# Revit family: Холодильные столы низкотемпературные
name_source: partatom
category: Оборудование
units: mm (PartAtom-declared; Revit-internal decimal feet)

## family parameters
Всегда вертикально = Да
Классификация = Нет
На основе рабочей плоскости = Нет
Общий = Нет
При загрузке вырезать с полостями = Нет
Размер круглого соединителя = Использовать диаметр
Тип детали = Нормальный
Точка расчета площади = Нет

## types (12) — shared parameters
Высота = 850 мм
Диап. рабочих темп. = -18
Напряжение питания = 230.00 В
Степень защиты = IP24
Терморегулятор = эл. блок
Тип оттайки = авт. с системой исп. конденсата
Тип охлаждения = динамический
Хладаген = R404A
Холодильный стол = нержавеющая сталь
zero-valued in all types: Отметка по умолчанию

## per-type parameters (varying)
| type | Боковая панель упр. | Боковая панель упр. (3 решетки) | Вес нетто/брутто, кг | Габаритные размеры, мм | Глубина | Дверь G - 1 | Дверь G-2 | Дверь G-3 | Дверь G-4 | Дверь GC | Количество дверей | Нижнее распол Дверь -1 | Нижнее распол. Дверь -2 | Нижняя панель упр. | Объем, л | Размеры в упоковке, мм | Столешница закругл. | Столешница квадр. | Таблица поиска | Условия окр. среды (темп/влажн) | Цена, руб | Число дверей | Ширина |
| TB4GN-GC | Да | Нет | 165/200 | 2060х705х850/910 | 705 мм | Нет | Нет | Нет | Нет | Да | 4 | Нет | Нет | Нет | 600 | 2165х815х1045 | Нет | Да | ТB | до +43/до 80 | 96 366 | 4 | 2060 мм |
| TBi4-G | Нет | Нет | - | 1850х600х850/910 | 600 мм | Нет | Нет | Нет | Нет | Нет | 4 | Да | Да | Да | 306 | 2000х714х1040 | Да | Нет | ТB | до +32 | 90 200 | 2 | 1850 мм |
| TBi-2G | Нет | Нет | - | 900х600х850/910 | 600 мм | Нет | Нет | Нет | Нет | Нет | 2 | Да | Нет | Да | 153 | 1045х714х1040 | Да | Нет | ТB | до +32 | 55 654 | 2 | 900 мм |
| TBi3-G | Нет | Нет | - | 1375х600х850/910 | 600 мм | Нет | Нет | Нет | Нет | Нет | 3 | Да | Нет | Да | 230 | 1520х714х1040 | Да | Нет | ТМ | до +32 | 74 046 | 2 | 1375 мм |
| TB2GN-G | Нет | Да | 130/150 | 1200х705х850/910 | 705 мм | Да | Да | Нет | Нет | Нет | 2 | Нет | Нет | Нет | 320 | 1310х815х1045 | Нет | Да | ТB | до +25/до 60 | 66 371 | 2 | 1200 мм |
| TB3GN-G | Нет | Да | 150/180 | 1630х705х850/910 | 705 мм | Да | Да | Нет | Да | Нет | 3 | Нет | Нет | Нет | 450 | 1725х815х1045 | Нет | Да | ТB | до +25/до 60 | 81 374 | 2 | 1630 мм |
| TB4GN-G | Нет | Да | 165/200 | 2060х705х850/910 | 705 мм | Да | Да | Да | Да | Нет | 4 | Нет | Нет | Нет | 600 | 2165х815х1045 | Нет | Да | ТB | до +25/до  60 | 99 631 | 2 | 2060 мм |
| TBi2GN-G | Нет | Нет | - | 900х700х850/910 | 700 мм | Нет | Нет | Нет | Нет | Нет | 2 | Да | Нет | Да | 184 | 1045х814х1040 | Да | Нет | ТB | до +32 | 57 045 | 2 | 900 мм |
| TBi3GN-G | Нет | Нет | - | 1375х700х850/910 | 700 мм | Нет | Нет | Нет | Нет | Нет | 3 | Да | Нет | Да | 276 | 1520х814х1040 | Да | Нет | ТМ | до +32 | 77 500 | 2 | 1375 мм |
| TBi4GN-G | Нет | Нет | - | 1850х700х850/910 | 700 мм | Нет | Нет | Нет | Нет | Нет | 4 | Да | Да | Да | 368 | 2000х714х1040 | Да | Нет | ТB | до +32 | 94 940 | 2 | 1850 мм |
| TB2GN-GC | Да | Нет | 130/150 | 1200х705х850/910 | 705 мм | Да | Да | Нет | Нет | Нет | 2 | Нет | Нет | Нет | 320 | 1310х815х1045 | Да | Нет | ТB | до +25/до 60 | 64 271 | 2 | 1200 мм |
| TB3GN-GC | Да | Нет | 150/180 | 1630х705х850/910 | 705 мм | Да | Да | Нет | Да | Нет | 3 | Нет | Нет | Нет | 450 | 1725х815х1045 | Да | Нет | ТB | до +25/до 60 | 78 376 | 2 | 1630 мм |
